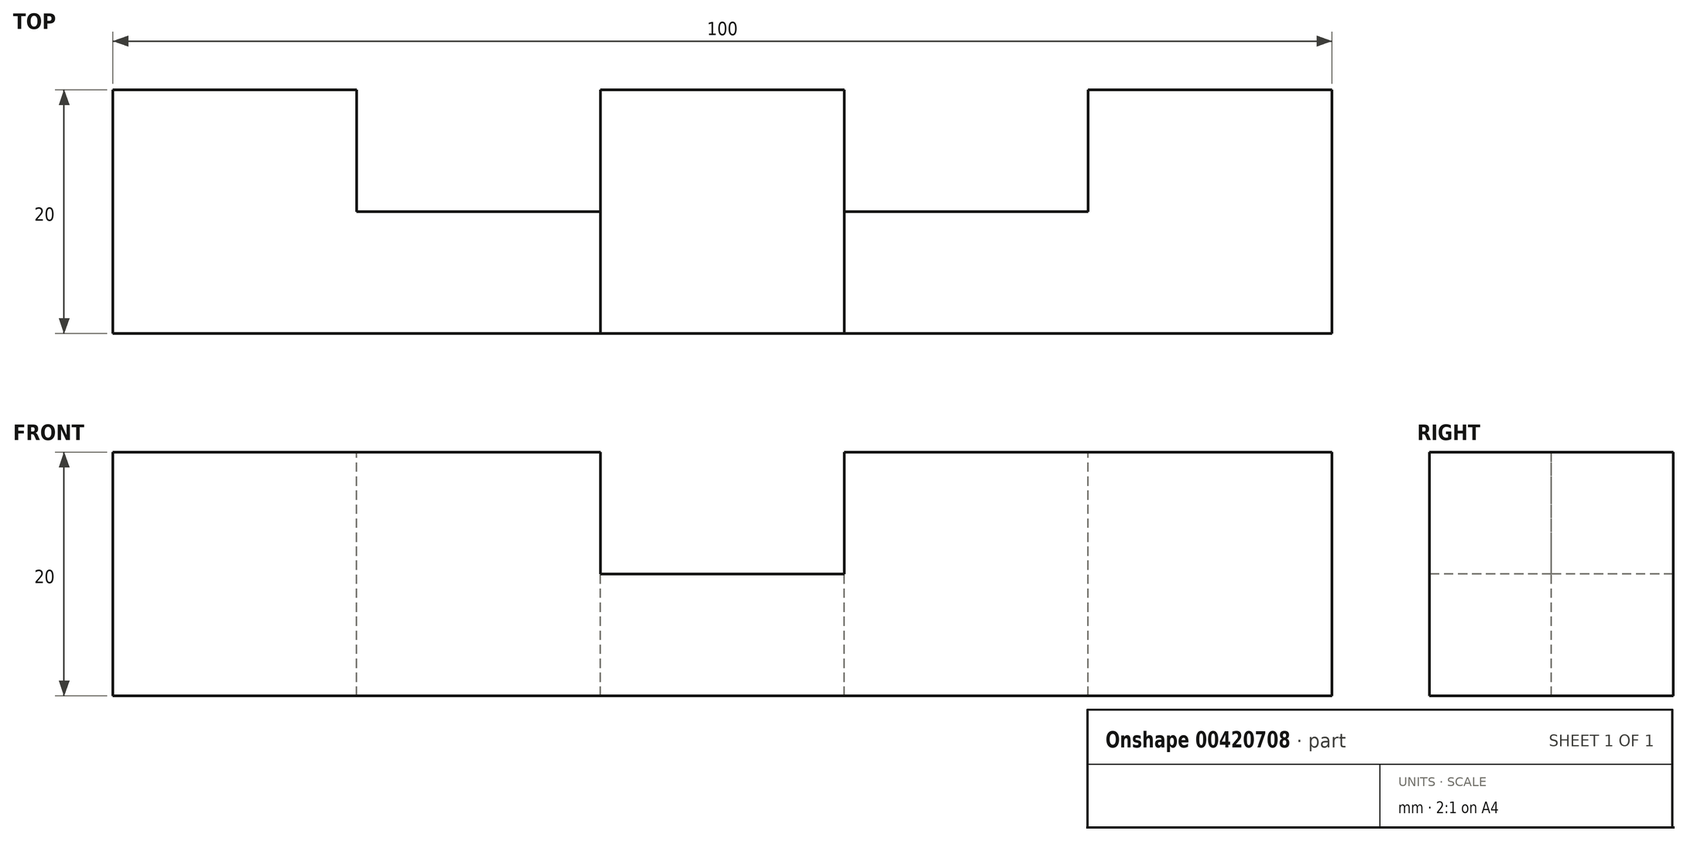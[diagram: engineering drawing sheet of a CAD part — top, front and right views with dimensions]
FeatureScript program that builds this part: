
annotation { "Feature Type Name" : "Feature", "Feature Type Description" : "" }
export const myFeature = defineFeature(function(context is Context, id is Id, definition is map)
    precondition{}
    {
        {
            var Q0;
            Q0=qCreatedBy(makeId("Right.planeOp"),FACE);
            var sketch = newSketch(context, id + "F0", { "sketchPlane" : qUnion([Q0])});
            skLineSegment(sketch, "E0.bottom", {"start": v(10, 10) * mm, "end": v(-10, 10) * mm});
            skLineSegment(sketch, "E0.top", {"start": v(10, -10) * mm, "end": v(-10, -10) * mm});
            skLineSegment(sketch, "E0.left", {"start": v(10, 10) * mm, "end": v(10, -10) * mm});
            skLineSegment(sketch, "E0.right", {"start": v(-10, 10) * mm, "end": v(-10, -10) * mm});
            skPoint(sketch, "E0.middle", {"position": v(0, 0) * mm});
            skSolve(sketch);
        }
        {
            var Q0;
            Q0=qSketchRegion(id+"F0",true);
            extrude(context, id + "F1", {"entities" : qUnion([Q0]), "endBound" : BoundingType.SYMMETRIC, "depth" : 100 * mm});
        }
        {
            var Q0;
            Q0=makeQuery(id+"F1.opExtrude","SWEPT_FACE",FACE,{"disambiguationData":[OSD([sQuery(id+"F0.wireOp",EDGE,"E0.right")])]});
            var sketch = newSketch(context, id + "F2", { "sketchPlane" : qUnion([Q0])});
            skLineSegment(sketch, "E1.bottom", {"start": v(-10, 10) * mm, "end": v(10, 10) * mm});
            skLineSegment(sketch, "E1.top", {"start": v(-10, 0) * mm, "end": v(10, 0) * mm});
            skLineSegment(sketch, "E1.left", {"start": v(-10, 10) * mm, "end": v(-10, 0) * mm});
            skLineSegment(sketch, "E1.right", {"start": v(10, 10) * mm, "end": v(10, 0) * mm});
            skSolve(sketch);
        }
        {
            var Q0;
            Q0=qSketchRegion(id+"F2",true);
            extrude(context, id + "F3", {"entities" : qUnion([Q0]), "operationType" : NewBodyOperationType.REMOVE, "oppositeDirection" : true, "depth" : 20 * mm});
        }
        {
            var Q0;
            {var subQ2=sQuery(id+"F0.wireOp",EDGE,"E0.bottom");Q0=makeQuery(id+"F3.boolean.opBoolean","SPLIT",FACE,{"disambiguationData":[TD([makeQuery(id+"F3.opExtrude","SWEPT_FACE",FACE,{"disambiguationData":[OSD([sQuery(id+"F2.wireOp",EDGE,"E1.right")])]})])],"derivedFrom":makeQuery(id+"F1.opExtrude","SWEPT_FACE",FACE,{"disambiguationData":[OSD([subQ2])]})});}
            var sketch = newSketch(context, id + "F4", { "sketchPlane" : qUnion([Q0])});
            skLineSegment(sketch, "E2.bottom", {"start": v(10, 10) * mm, "end": v(30, 10) * mm});
            skLineSegment(sketch, "E2.top", {"start": v(10, 0) * mm, "end": v(30, 0) * mm});
            skLineSegment(sketch, "E2.left", {"start": v(10, 10) * mm, "end": v(10, 0) * mm});
            skLineSegment(sketch, "E2.right", {"start": v(30, 10) * mm, "end": v(30, 0) * mm});
            skLineSegment(sketch, "E3.bottom", {"start": v(-10, 10) * mm, "end": v(-30, 10) * mm});
            skLineSegment(sketch, "E3.top", {"start": v(-10, 0) * mm, "end": v(-30, 0) * mm});
            skLineSegment(sketch, "E3.left", {"start": v(-10, 10) * mm, "end": v(-10, 0) * mm});
            skLineSegment(sketch, "E3.right", {"start": v(-30, 10) * mm, "end": v(-30, 0) * mm});
            skSolve(sketch);
        }
        {
            var Q0;
            Q0 = qSketchRegion(id + "F4", true);
            extrude(context, id + "F5", {"entities" : qUnion([Q0]), "operationType" : NewBodyOperationType.REMOVE, "oppositeDirection" : true, "depth" : 20 * mm});
        }
    });
